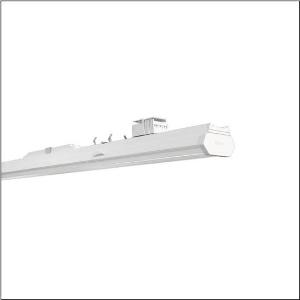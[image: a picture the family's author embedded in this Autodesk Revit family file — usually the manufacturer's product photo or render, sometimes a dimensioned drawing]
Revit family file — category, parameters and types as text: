
# Revit family: licross_r__21_protected_ho_52td13mn4fxs_5700
name_source: partatom
category: Lighting Fixtures
units: mm (PartAtom-declared; Revit-internal decimal feet)

## family parameters
Cut with Voids When Loaded = No
Host = Face
Light Source = No
Part Type = Normal
Room Calculation Point = No
Round Connector Dimension = Use Diameter
Shared = No

## types (1)
- --- (1 x LED, 15060 lm, 83.2 W, 4000K)
    Apparent Load = 83 VA
    CIE Flux Codes = 89 96 99 100 99
    Color Rendering = 80
    Color Temperature = 4000K
    Default Elevation = 1800 mm
    Description = Licross® 21 Protected HO, luminaire insert, of sheet steel, galvanised, coil coated, white, length: 1.500mm, width: 66mm, height: 67mm, LED rated luminous flux: 15.060lm, light colour: 840, SDCM (Standard Deviation of Colour Matching)MacAdam ≤ 3 SDCM (initial), control gear: ON/OFF Multilumen, with plug, 3-pole, with phase selection, mains connection: 220..240V, AC, 50/60Hz, rated input power: 83W, internal wiring halogen-free, primary light control with lens, of plastic, primary optical cover: cover, of PMMA, light emission: direct distribution, primary light characteristic: symmetric, protection rating (complete): IP54, insulation class (complete): insulation class I (protective earthing), certification: CE, ENEC, VDE, UKCA, protection symbol: D if used in an environment with non-conductive dust loads with corresponding accessories, impact resistance: IK06, permissible ambient temperature for indoor applications: -35..+35°C, corresponds to IFS (International Featured Standards) requirements for safety and quality in the food industry, reducing of maximum allowable ambient temperature of 5°C with ceiling mounting, LABS conformity tested according to VDMA 24364:2018-05, packaging unit: 1 piece
    Height = 92 mm
    Lamp = 1 x LED
    Lamp Light Flux = 15060 lm
    Lamp Power = 83.2 W
    Lamp count = 1
    Length = 1500 mm
    Luminous efficacy = 181 lm/W
    Manufacturer = Siteco
    ModVariant = No
    Model = 52TD13MN4FXS
    Mounting Place = Ceiling
    Mounting Type = Pendant
    Number of Poles = 1
    OnlyDefault = Yes
    Power Factor = 1
    Product Name = Licross® 21 Protected HO
    Product group = luminaire insert | ceiling pendant
    ProductGroupID = 901
    Protection Class = Protection class I
    Protection Degree = IP 54
    RLX_Detail_Level = 1
    RLX_Emergency_Light_Flux = 0 lm
    RLX_Emergency_Type = 0
    RLX_Emergency_Type_DB = No
    RlxData = <blob elided: 22057 chars, md5=024b52b3>
    Socket = socket
    Standby Power = 0 W
    System Light Flux = 15060 lm
    System Power = 83 W
    Type Comments = factory setting: luminous flux: 100 % | (A | C | E) | 195 mA
    Type Image = l_1256148.jpg
    URL = http://relux.com
    VarID = @adj_112949
    Voltage = 0 V
    Weight = 0.00 kg
    Width = 88 mm

## geometry (parser evidence)
native form markers: Blend x4, Sweep x11
no freeform markers — native parametric forms only
